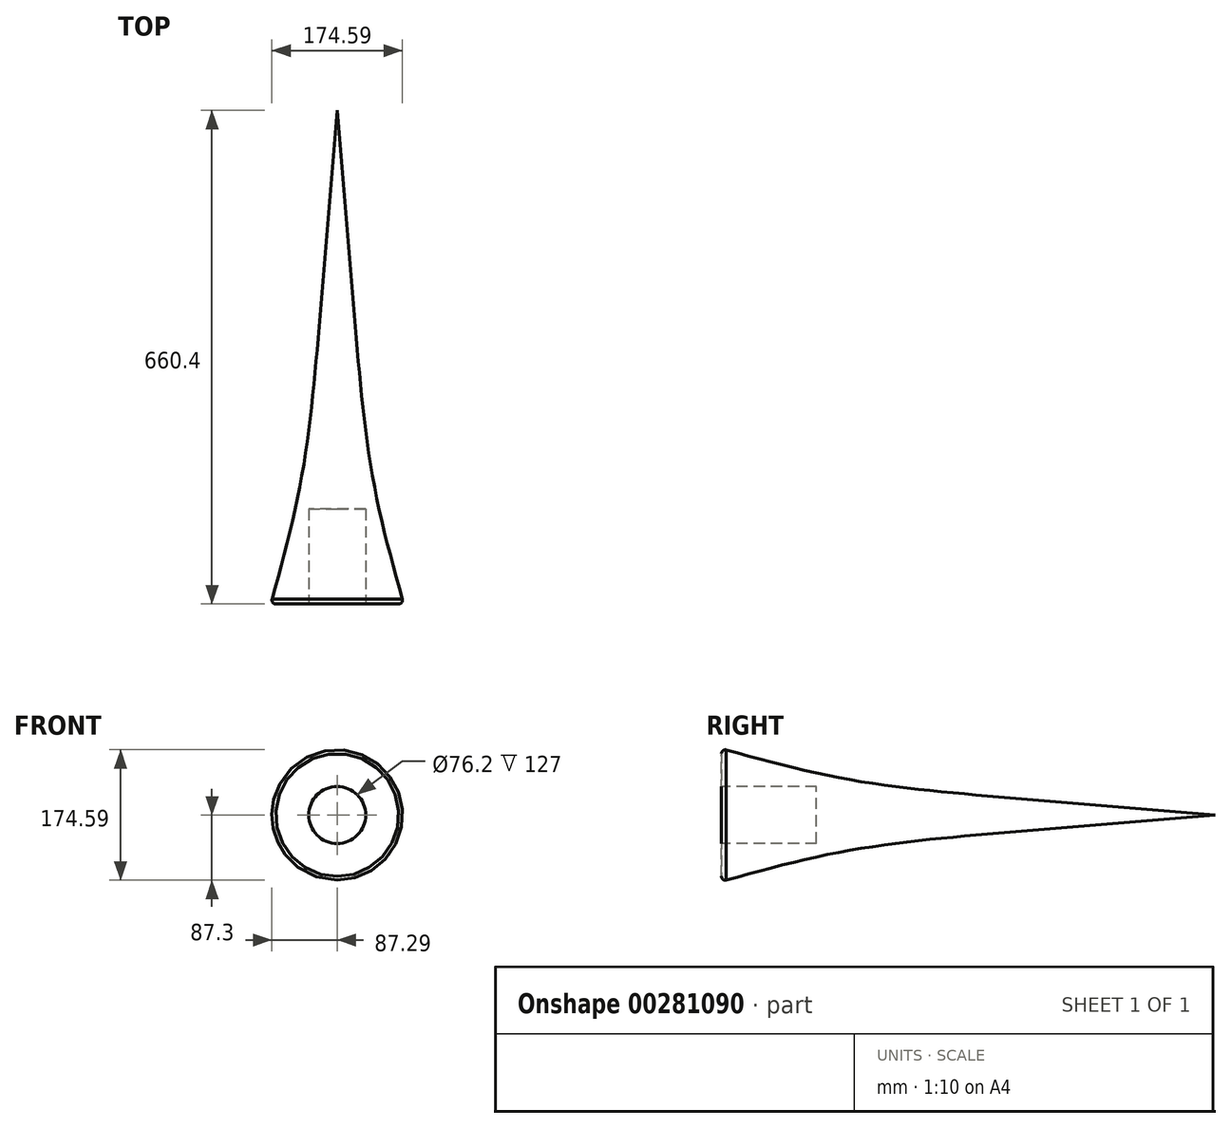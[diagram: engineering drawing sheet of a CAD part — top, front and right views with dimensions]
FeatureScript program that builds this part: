
annotation { "Feature Type Name" : "Feature", "Feature Type Description" : "" }
export const myFeature = defineFeature(function(context is Context, id is Id, definition is map)
    precondition{}
    {
        {
            var Q0;
            Q0=qCreatedBy(makeId("Front.planeOp"),FACE);
            var sketch = newSketch(context, id + "F0", { "sketchPlane" : qUnion([Q0])});
            skCircle(sketch, "E0", {"center": v(0, 0) * mm, "radius": 50.8 * mm});
            skSolve(sketch);
        }
        {
            var Q0;
            Q0=qCreatedBy(makeId("Front.planeOp"),FACE);
            cPlane(context, id + "F1", {"entities" : qUnion([Q0]), "cplaneType" : CPlaneType.OFFSET, "offset" : 152.4 * mm, "width" : 152.4 * mm, "height" : 152.4 * mm});
        }
        {
            var Q0;
            Q0=qCreatedBy(makeId("Front.planeOp"),FACE);
            cPlane(context, id + "F2", {"entities" : qUnion([Q0]), "cplaneType" : CPlaneType.OFFSET, "offset" : 203.2 * mm, "oppositeDirection" : true, "width" : 152.4 * mm, "height" : 152.4 * mm});
        }
        {
            var Q0;
            Q0=qCreatedBy(id+"F1.planeOp",FACE);
            var sketch = newSketch(context, id + "F3", { "sketchPlane" : qUnion([Q0])});
            skCircle(sketch, "E1", {"center": v(0, 0) * mm, "radius": 88.9 * mm});
            skSolve(sketch);
        }
        {
            var Q0;
            Q0=qCreatedBy(id+"F2.planeOp",FACE);
            var sketch = newSketch(context, id + "F4", { "sketchPlane" : qUnion([Q0])});
            skCircle(sketch, "E2", {"center": v(0, 0) * mm, "radius": 25.4 * mm});
            skSolve(sketch);
        }
        {
            var Q0;
            Q0=makeQuery(id+"F3.imprint","IMPRINT",FACE,{"disambiguationData":[TD([[makeQuery(id+"F3.imprint","IMPRINT",EDGE,{"derivedFrom":sQuery(id+"F3.wireOp",EDGE,"E1")}),1.0]])]});
            var Q1;
            Q1=makeQuery(id+"F0.imprint","IMPRINT",FACE,{"disambiguationData":[TD([[makeQuery(id+"F0.imprint","IMPRINT",EDGE,{"derivedFrom":sQuery(id+"F0.wireOp",EDGE,"E0")}),1.0]])]});
            var Q2;
            Q2=makeQuery(id+"F4.imprint","IMPRINT",FACE,{"disambiguationData":[TD([[makeQuery(id+"F4.imprint","IMPRINT",EDGE,{"derivedFrom":sQuery(id+"F4.wireOp",EDGE,"E2")}),1.0]])]});
            loft(context, id + "F5", {"sheetProfilesArray" : [{ "sheetProfileEntities" : qUnion([Q0]) }, { "sheetProfileEntities" : qUnion([Q1]) }, { "sheetProfileEntities" : qUnion([Q2]) }]});
        }
        {
            var Q0;
            Q0=qCreatedBy(makeId("Front.planeOp"),FACE);
            cPlane(context, id + "F6", {"entities" : qUnion([Q0]), "cplaneType" : CPlaneType.OFFSET, "offset" : 508 * mm, "oppositeDirection" : true, "width" : 152.4 * mm, "height" : 152.4 * mm});
        }
        {
            var Q0;
            Q0=qCreatedBy(id+"F6.planeOp",FACE);
            var sketch = newSketch(context, id + "F7", { "sketchPlane" : qUnion([Q0])});
            skCircle(sketch, "E3", {"center": v(0, 0) * mm, "radius": 10.16 * mm});
            skSolve(sketch);
        }
        {
            var Q1;
            Q1=makeQuery(id+"F5.opLoft","CAP_FACE",FACE,{"disambiguationData":[OSD([makeQuery(id+"F4.imprint","IMPRINT",FACE,{"disambiguationData":[TD([[makeQuery(id+"F4.imprint","IMPRINT",EDGE,{"derivedFrom":sQuery(id+"F4.wireOp",EDGE,"E2")}),1.0]])]})])],"isStart":true});
            var Q2;
            Q2=sQuery(id+"F7.wireOp",VERTEX,"E3.center");
            loft(context, id + "F8", {"operationType" : NewBodyOperationType.ADD, "sheetProfilesArray" : [{ "sheetProfileEntities" : qUnion([Q1]) }, { "sheetProfileEntities" : qUnion([Q2]) }]});
        }
        {
            var Q0;
            Q0=qCreatedBy(id+"F1.planeOp",FACE);
            var sketch = newSketch(context, id + "F9", { "sketchPlane" : qUnion([Q0])});
            skCircle(sketch, "E4", {"center": v(0, 0) * mm, "radius": 38.1 * mm});
            skSolve(sketch);
        }
        {
            var Q0;
            Q0=makeQuery(id+"F9.imprint","IMPRINT",FACE,{"disambiguationData":[TD([[makeQuery(id+"F9.imprint","IMPRINT",EDGE,{"derivedFrom":sQuery(id+"F9.wireOp",EDGE,"E4")}),1.0]])]});
            extrude(context, id + "F10", {"entities" : qUnion([Q0]), "operationType" : NewBodyOperationType.REMOVE, "oppositeDirection" : true, "depth" : 127 * mm});
        }
        {
            var Q0;
            Q0=makeQuery(id+"F5.opLoft","MID_CAP_EDGE",EDGE,{"disambiguationData":[OSD([sQuery(id+"F3.wireOp",EDGE,"E1")])],"capPos":0.0});
            var Q1;
            Q1=makeQuery(id+"F10.boolean.opBoolean","COPY",EDGE,{"derivedFrom":makeQuery(id+"F10.opExtrude","CAP_EDGE",EDGE,{"disambiguationData":[OSD([sQuery(id+"F9.wireOp",EDGE,"E4")])],"isStart":true})});
            fillet(context, id + "F11", {"entities" : qUnion([Q0, Q1]), "radius" : 5.08 * mm, "tangentPropagation" : true, "allowEdgeOverflow" : false});
        }
    });
